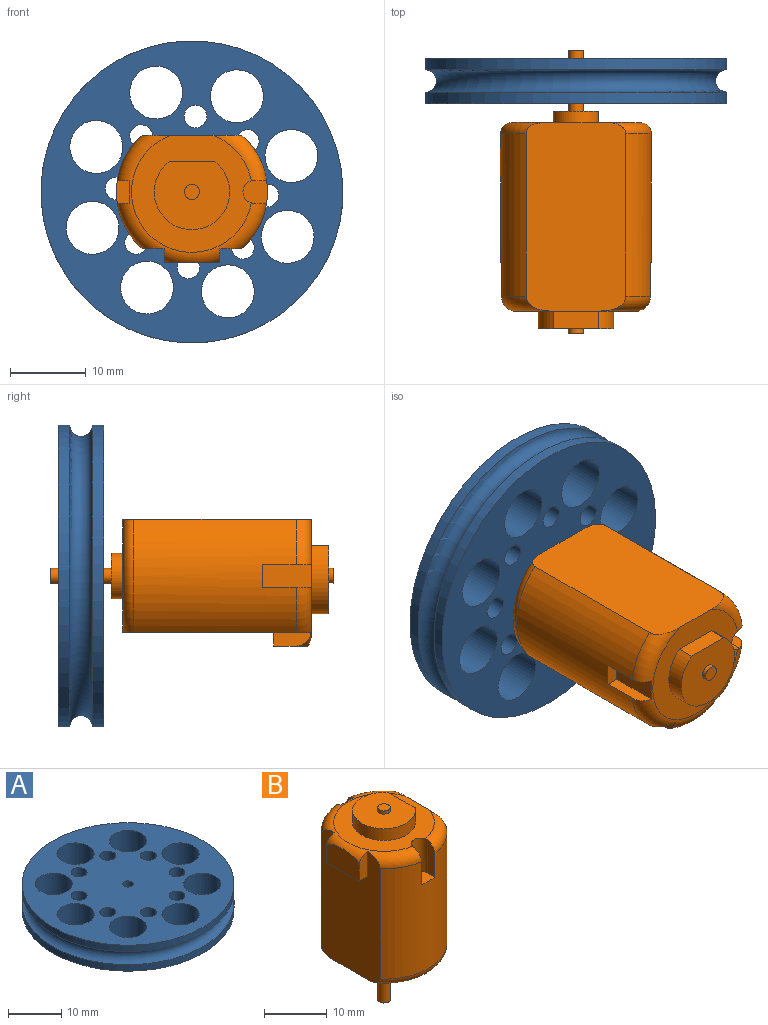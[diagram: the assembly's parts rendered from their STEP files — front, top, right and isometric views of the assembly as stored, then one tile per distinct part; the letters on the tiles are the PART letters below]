
ASSEMBLY  parts=2 mates=1
PART A: 22 faces, bbox 45.6x45.6x6 mm
  f0: cylinder r=20mm len=40mm, axis (0,0,-1), area 188.5mm2, adj f3,f21
  f1: cylinder r=20mm len=40mm, axis (0,0,-1), area 188.5mm2, adj f4,f21
  f2: cylinder r=1mm len=6mm, axis (0,0,-1), area 37.7mm2, adj f3,f4
  f3: plane 40x40mm, normal (0,0,1), area 889.1mm2, adj f0,f2,f5,f6,f7,f8,f9,f10
  f4: plane 40x40mm, normal (0,0,-1), area 889.1mm2, adj f1,f2,f5,f6,f7,f8,f9,f10
  f5: cylinder r=3.5mm len=7mm, axis (0,0,1), area 131.9mm2, adj f3,f4
  f6: cylinder r=3.5mm len=7mm, axis (0,0,1), area 131.9mm2, adj f3,f4
  f7: cylinder r=3.5mm len=7mm, axis (0,0,1), area 131.9mm2, adj f3,f4
  f8: cylinder r=3.5mm len=7mm, axis (0,0,1), area 131.9mm2, adj f3,f4
  f9: cylinder r=3.5mm len=7mm, axis (0,0,1), area 131.9mm2, adj f3,f4
  f10: cylinder r=3.5mm len=7mm, axis (0,0,1), area 131.9mm2, adj f3,f4
  f11: cylinder r=3.5mm len=7mm, axis (0,0,1), area 131.9mm2, adj f3,f4
  f12: cylinder r=3.5mm len=7mm, axis (0,0,1), area 131.9mm2, adj f3,f4
  f13: cylinder r=1.5mm len=6mm, axis (0,0,1), area 56.5mm2, adj f3,f4
  f14: cylinder r=1.5mm len=6mm, axis (0,0,1), area 56.5mm2, adj f3,f4
  f15: cylinder r=1.5mm len=6mm, axis (0,0,1), area 56.5mm2, adj f3,f4
  f16: cylinder r=1.5mm len=6mm, axis (0,0,1), area 56.5mm2, adj f3,f4
  f17: cylinder r=1.5mm len=6mm, axis (0,0,1), area 56.5mm2, adj f3,f4
  f18: cylinder r=1.5mm len=6mm, axis (0,0,1), area 56.5mm2, adj f3,f4
  f19: cylinder r=1.5mm len=6mm, axis (0,0,1), area 56.5mm2, adj f3,f4
  f20: cylinder r=1.5mm len=6mm, axis (0,0,1), area 56.5mm2, adj f3,f4
  f21: torus R=20mm, axis (0,0,1), area 563.9mm2, adj f0,f1
PART B: 32 faces, bbox 21.1x21.8x37.5 mm
  f0: plane 15.87x15.5mm, normal (0,0,1), area 122.1mm2, adj f4,f10,f11,f27,f30,f31
  f1: cylinder r=10mm len=21.5mm, axis (0,0,-1), area 351.1mm2, adj f4,f5,f24,f25,f26,f28,f30,f31
  f2: cylinder r=10mm len=21.5mm, axis (0,0,-1), area 351.1mm2, adj f4,f5,f20,f21,f22,f29,f30
  f3: plane 17x15mm, normal (0,0,-1), area 187.9mm2, adj f4,f5,f6,f28,f29
  f4: plane 25x13.23mm, normal (1,0,0), area 326.4mm2, adj f0,f1,f2,f3,f28,f29,f30,f31
  f5: plane 24.97x13.23mm, normal (-1,0,0), area 289.4mm2, adj f1,f2,f3,f15,f18,f19,f28,f29
  f6: cylinder r=3mm len=6mm, axis (0,0,1), area 28.3mm2, adj f3,f7
  f7: plane 6x6mm, normal (0,0,-1), area 25.1mm2, adj f6,f8
  f8: cylinder r=1mm len=8mm, axis (0,0,1), area 50.3mm2, adj f7,f9
  f9: plane 2x2mm, normal (0,0,-1), area 3.1mm2, adj f8
  f10: plane 6x2.3mm, normal (1,0,0), area 13.8mm2, adj f0,f11,f12
  f11: cylinder r=5mm len=10mm, axis (0,0,-1), area 57.5mm2, adj f0,f10,f12
  f12: plane 10x9mm, normal (0,0,1), area 71.3mm2, adj f10,f11,f13
  f13: cylinder r=1mm len=2mm, axis (0,0,-1), area 3.8mm2, adj f12,f14
  f14: plane 2x2mm, normal (0,0,1), area 3.1mm2, adj f13
  f15: plane 4.97x1.79mm, normal (0,1,0), area 8mm2, adj f5,f16,f19,f30
  f16: cylinder r=10mm len=3mm, axis (0,0,1), area 0.2mm2, adj f15,f17,f19,f30
  f17: plane 7.33x4.52mm, normal (-1,0,0), area 30.9mm2, adj f16,f18,f19,f30
  f18: plane 4.97x1.79mm, normal (0,-1,0), area 8mm2, adj f5,f17,f19,f30
  f19: plane 7.4x1.82mm, normal (0,0,-1), area 13.3mm2, adj f5,f15,f16,f17,f18
  f20: plane 6.46x1.64mm, normal (-1,0,0), area 9.8mm2, adj f2,f22,f23,f30
  f21: plane 6.46x1.64mm, normal (1,0,0), area 9.8mm2, adj f2,f22,f23,f30
  f22: plane 3x1.75mm, normal (0,0,1), area 5.1mm2, adj f2,f20,f21,f23
  f23: plane 6.48x3mm, normal (0,1,0), area 19.4mm2, adj f20,f21,f22,f30
  f24: plane 6.46x1.64mm, normal (1,0,0), area 9.8mm2, adj f1,f26,f27,f30
  f25: plane 6.6x1.78mm, normal (-1,0,0), area 9.8mm2, adj f1,f26,f27,f31
  f26: plane 3.25x3mm, normal (0,0,1), area 8.7mm2, adj f1,f24,f25,f27
  f27: cylinder r=1.5mm len=6.5mm, axis (0,0,1), area 30.6mm2, adj f0,f24,f25,f26,f30,f31
  f28: torus R=8.5mm, axis (0,0,1), area 41mm2, adj f1,f3,f4,f5
  f29: torus R=8.5mm, axis (0,0,1), area 41mm2, adj f2,f3,f4,f5
  f30: torus R=8mm, axis (0,0,1), area 83.3mm2, adj f0,f1,f2,f4,f5,f15,f16,f17
  f31: torus R=8mm, axis (0,0,1), area 22.8mm2, adj f0,f1,f4,f25,f27
PLACE A rot(axis=(0.74,-0.47,0.47),106.7deg) t=(0,20.95,-7.5)mm
PLACE B rot(axis=(0.58,-0.58,0.58),120deg) t=(0,12.45,-7.5)mm
MATE revolute A.f2 <-> B.f8  axis (0,1,0) through (0,17.95,-7.5)mm
